# Revit family: Haworth_ComposeStorage_StorageBox2
name_source: partatom
category: Furniture Systems
revit_build: Autodesk Revit 2018 (Build: 20170223_1515(x64)
units: mm (PartAtom-declared; Revit-internal decimal feet)

## family parameters
Always vertical = Yes
Cut with Voids When Loaded = No
OmniClass Number = 23.40.70.14.64.21
OmniClass Title = Systems Furniture
Part Type = Normal
Room Calculation Point = No
Round Connector Dimension = Use Diameter
Shared = No
Work Plane-Based = No

## types (1)
- Wall Mounted Storage Box - 96w
    Actual Depth = 15 5/8"
    Actual Height = 21 5/8"
    Actual Width = 72"
    Assembly Code = E2020200
    Box Width = 17 13/16"
    Cabinet Finish = Haworth _ Wood _ White Oak
    Center Vertical = Yes
    Description = Haworth - Compose - Wall Mounted Storage Box
    Door 2 Right Edge = 1/4"
    Door Width = 35 3/4"
    Door2 = Yes
    Edge Finish = Haworth _ Wood _ White Oak
    Manufacturer = Haworth
    Model = Haworth - Compose - Wall Mounted Storage Box
    Revision Number = 4
    Size = Verify Final Dim. w/ Haworth
    Standard Widths = 48, 60, 66, 72 in.
    Sustainability Info = http://media.haworth.com
    URL = www.haworth.com
    URL - Product = http://www.haworth.com
    Warranty = http://www.haworth.com
    Width = 72"

## geometry (parser evidence)
native form markers: Sweep x3
no freeform markers — native parametric forms only
